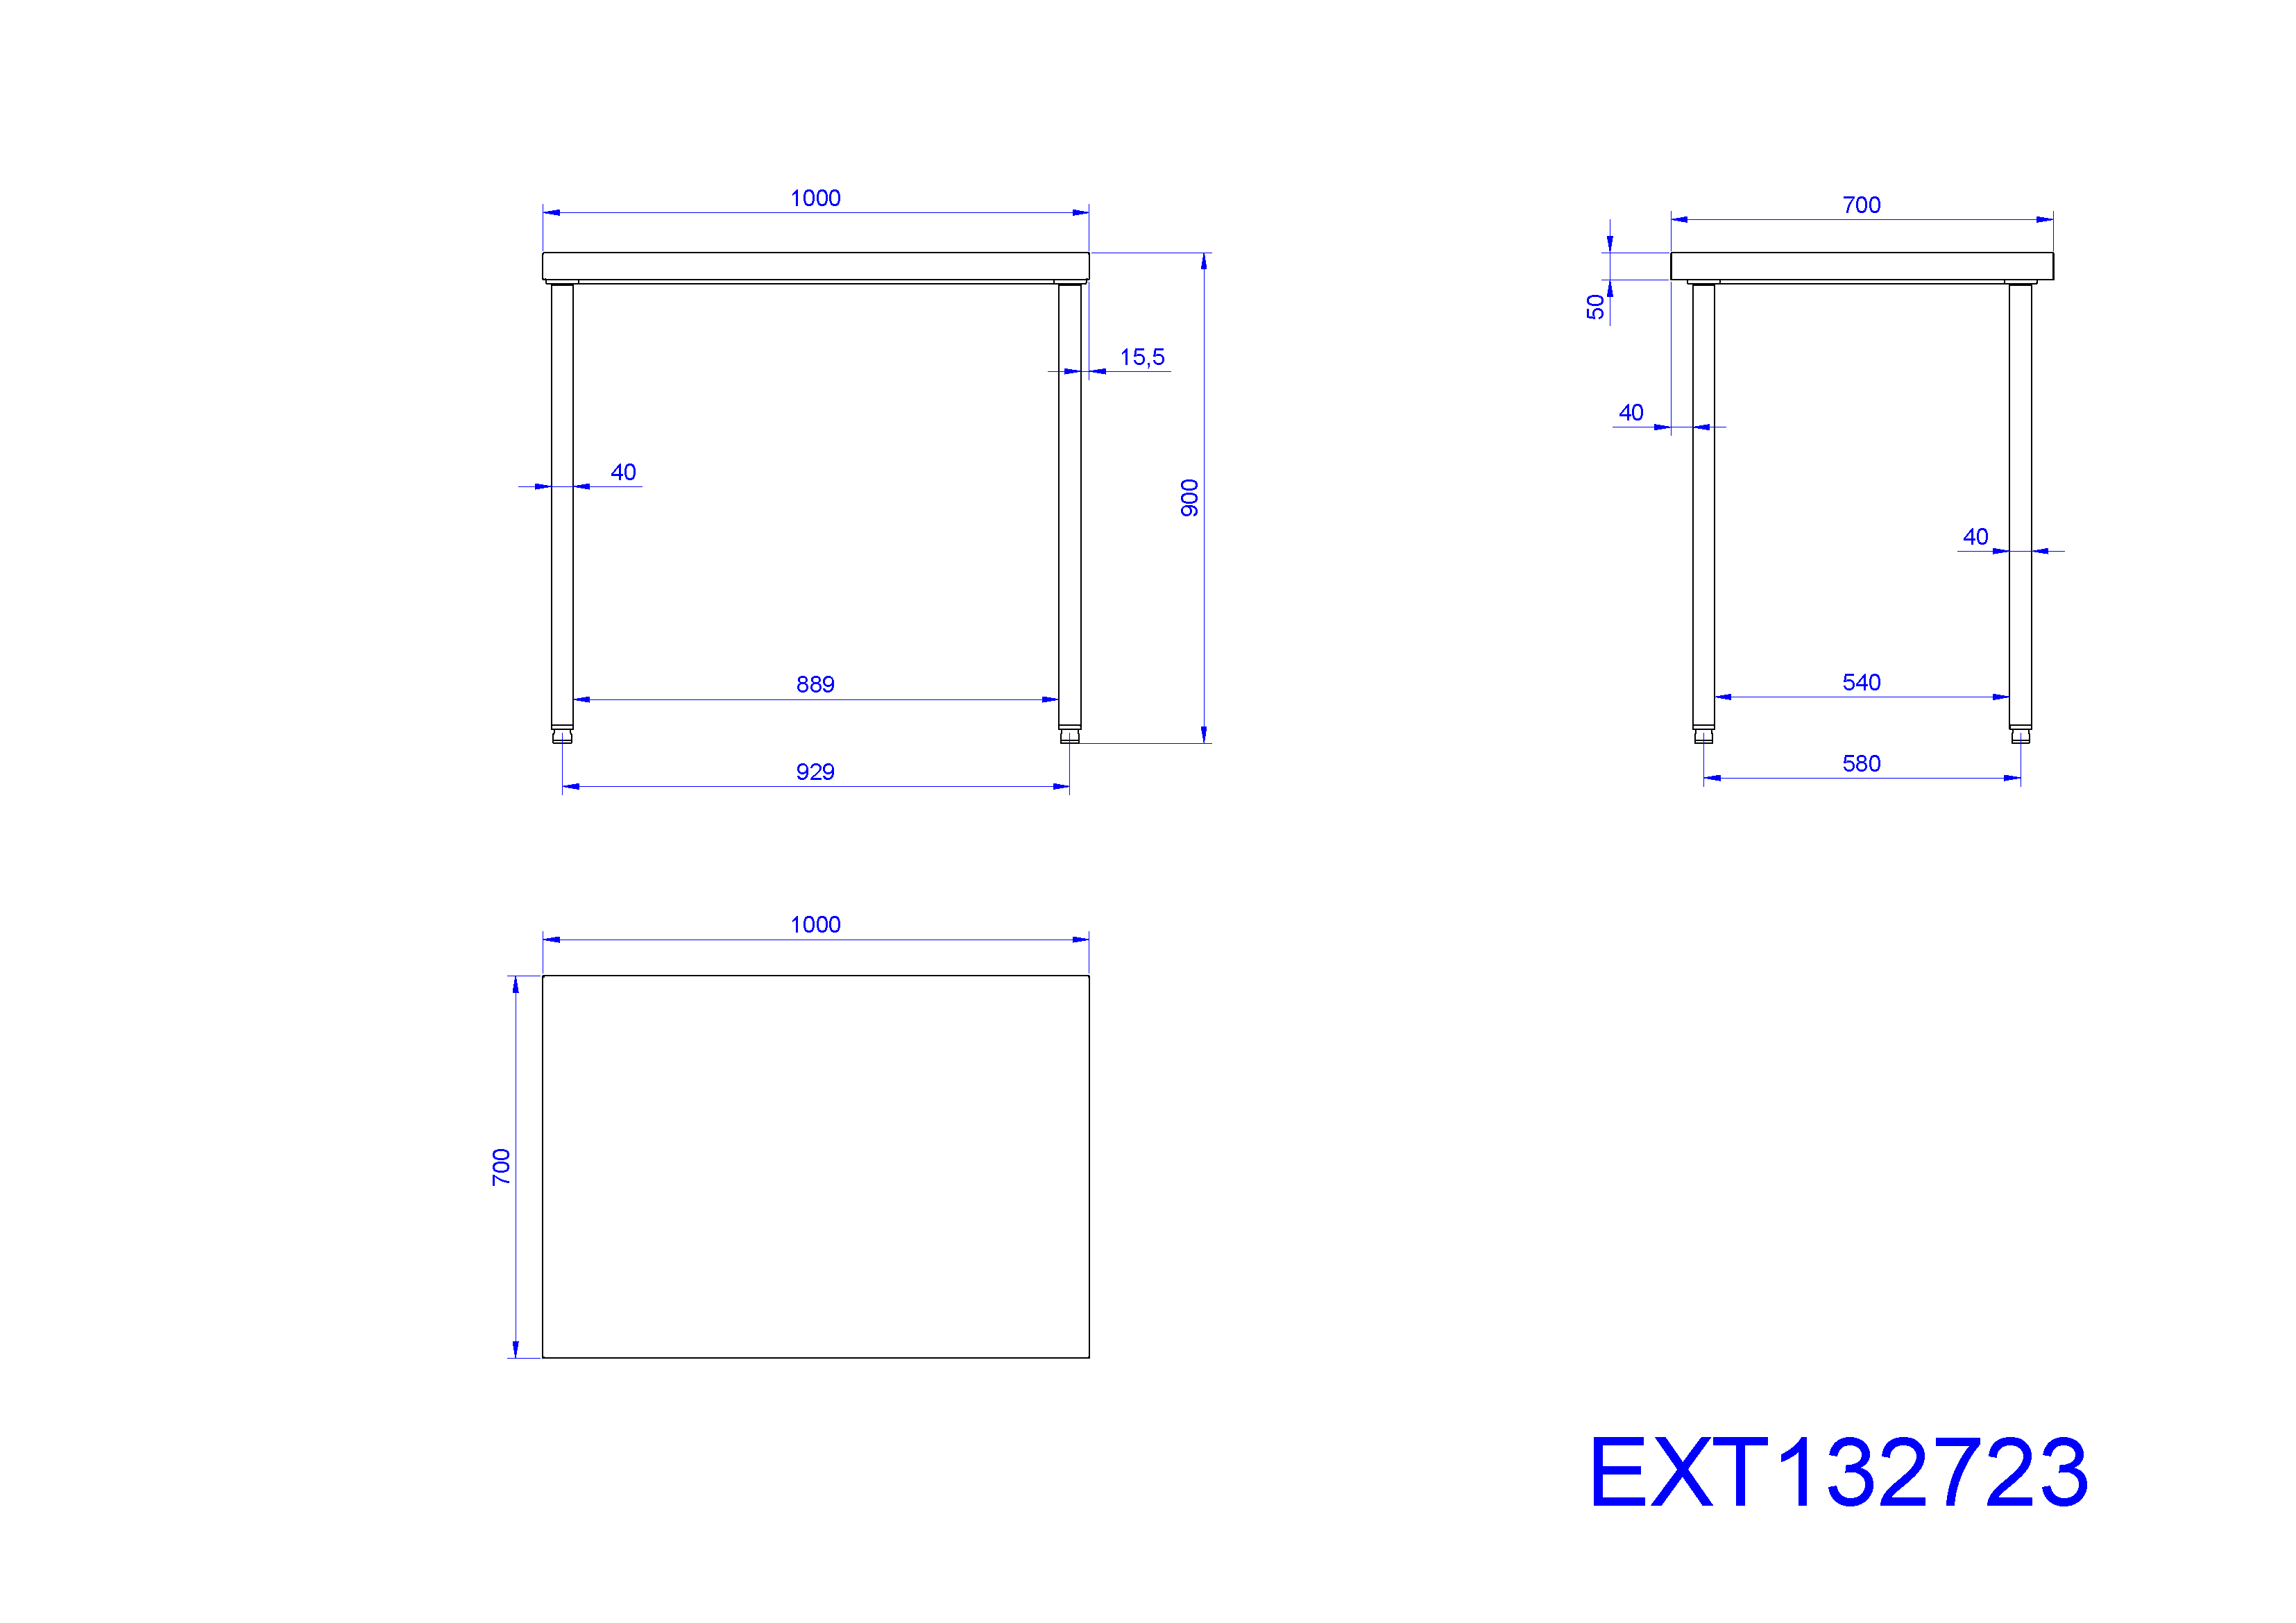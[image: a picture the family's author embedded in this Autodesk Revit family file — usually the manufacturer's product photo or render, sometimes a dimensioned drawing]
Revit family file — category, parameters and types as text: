
# Revit family: QF_ZANUSSI_132725_TG1400PN
name_source: partatom
category: Attrezzature speciali
units: mm (PartAtom-declared; Revit-internal decimal feet)

## family parameters
Basato su piano di lavoro = No
Condiviso = No
Punto di calcolo locali = No
Quota connettore circolare = Usa diametro
Sempre verticale = Sì
Taglio con vuoti quando caricato = No
Tipo di parte = Normale

## types (1)
- Standard
    Accessory = Sì
    Cold Water Size = 0 mm
    Compressed Air Pressure = 0.0 Pa
    Compressed Air Size = 0 mm
    Compressed Air Volume = 0.0 L/s
    Condensate Return Size = 0 mm
    Cycle = 0 Hz
    Depth Actual = 700 mm  [stored 2.29659 ft]
    Descrizione = WORK TABLE 1400 MM
    Direct Waste Size = 0 mm
    Gas Input Pressure = 0
    Gas KW = 0
    Gas Size = 0 mm
    HP = 0 HP
    Height Actual = 900 mm  [stored 2.95276 ft]
    Hot Water Size = 0 mm
    Item Number = 132725
    Length Actual = 1400 mm  [stored 4.59318 ft]
    Modello = TG1400PN
    Phase = 0
    Produttore = Zanussi
    Prospetto di default = 0 mm  [stored 0 ft]
    Refrigerant Compressor Remote = Sì
    Refrigeration Liquid Line Size = 0 mm  [stored 0 ft]
    Refrigeration Suction Line Size = 0 mm  [stored 0 ft]
    Steam Consumption per Hour = 0
    Steam Supply Maximum Pressure = 0.0 Pa
    Steam Supply Minimum Pressure = 0.0 Pa
    Steam Supply Size = 0 mm
    URL = http://www.zanussiprofessional.com
    URL Manufacturer = http://www.zanussiprofessional.com
    Volts = 0 V
    Watts = 0 W
    Weight = 33.00 kg

note: source unit labels omitted for Gas Input Pressure — the stored unit's dimension contradicts the parameter name (converter mislabeling)

note: [stored X ft] marks values corroborated as IEEE doubles in the binary element streams (Revit-internal decimal feet)

## geometry (parser evidence)
native form markers: Sweep x2
no freeform markers — native parametric forms only
